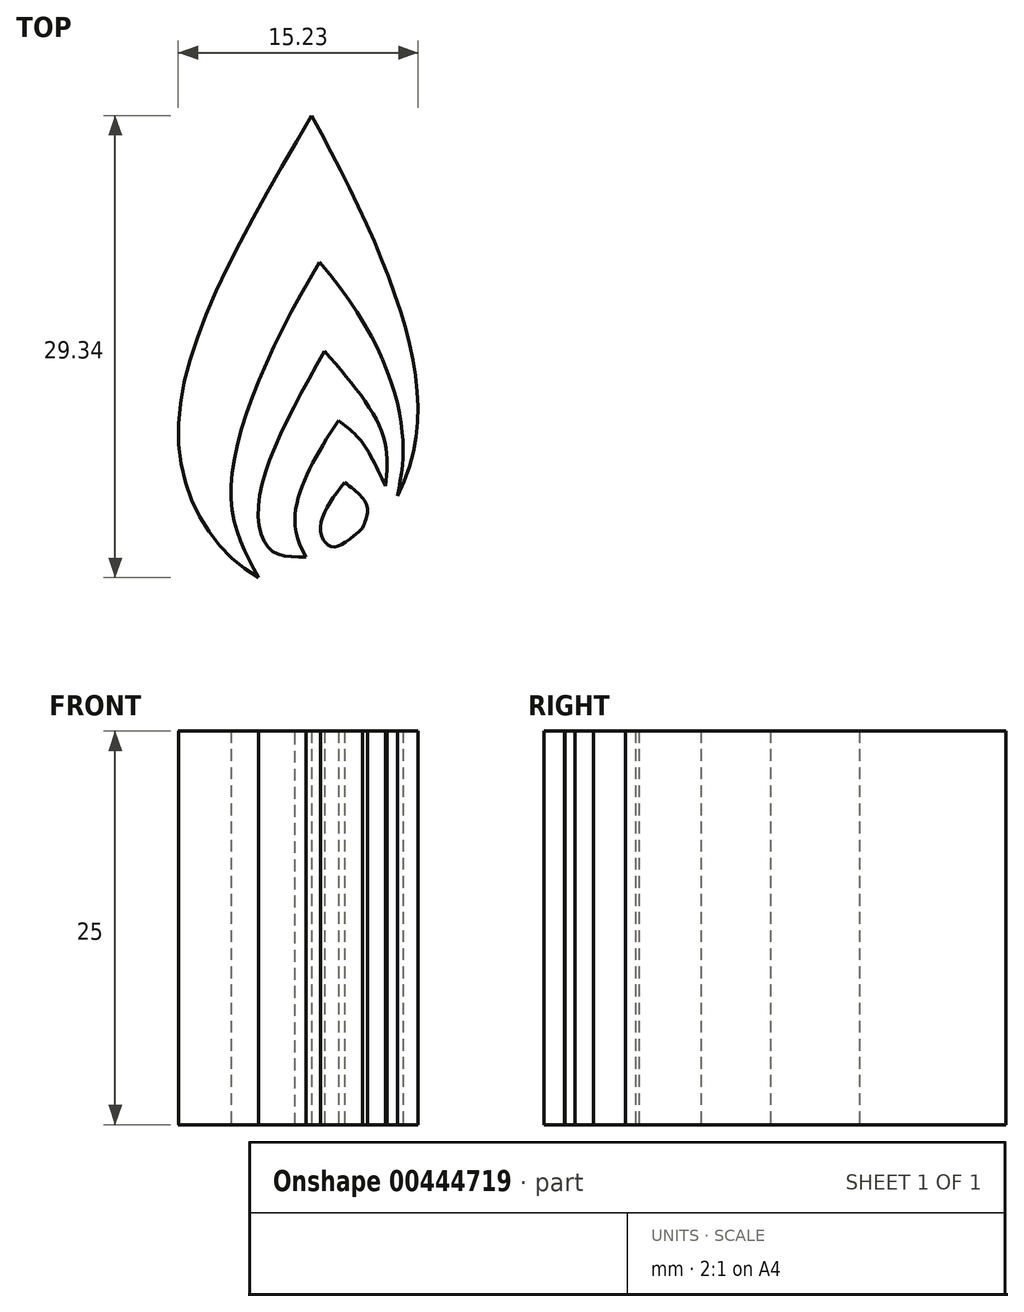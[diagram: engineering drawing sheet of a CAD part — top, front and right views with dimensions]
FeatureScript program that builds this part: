
annotation { "Feature Type Name" : "Feature", "Feature Type Description" : "" }
export const myFeature = defineFeature(function(context is Context, id is Id, definition is map)
    precondition{}
    {
        {
            var Q0;
            Q0=qCreatedBy(makeId("Top.planeOp"),FACE);
            var sketch = newSketch(context, id + "F0", { "sketchPlane" : qUnion([Q0])});
            skFitSpline(sketch, "E0", {"points": [v(-21.54, 31.4) * mm, v(-30, 10.88) * mm, v(-24.9, 2.05) * mm], "startDerivative": vector(-22.17, -38.16) * mm, "endDerivative": vector(20.91, -11.63) * mm});
            skFitSpline(sketch, "E1", {"points": [v(-21.54, 31.4) * mm, v(-15.36, 17.1) * mm, v(-16.09, 7.23) * mm], "startDerivative": vector(14.64, -26.64) * mm, "endDerivative": vector(-11.02, -21.44) * mm});
            skFitSpline(sketch, "E2", {"points": [v(-24.9, 2.05) * mm, v(-26.64, 7.68) * mm, v(-21.02, 22.09) * mm], "startDerivative": vector(-7.2, 13.11) * mm, "endDerivative": vector(14.41, 23.6) * mm});
            skFitSpline(sketch, "E3", {"points": [v(-21.02, 22.09) * mm, v(-15.84, 11.85) * mm, v(-16.09, 7.23) * mm], "startDerivative": vector(16.12, -18.6) * mm, "endDerivative": vector(-2.41, -10.96) * mm});
            skFitSpline(sketch, "E4", {"points": [v(-20.7, 16.43) * mm, v(-24.85, 7.1) * mm, v(-24.1, 3.78) * mm, v(-21.88, 3.37) * mm], "startDerivative": vector(-11.59, -20.64) * mm, "endDerivative": vector(10.8, 0.23) * mm});
            skFitSpline(sketch, "E5", {"points": [v(-20.7, 16.43) * mm, v(-17.04, 11.25) * mm, v(-16.83, 7.86) * mm], "startDerivative": vector(8.03, -9.25) * mm, "endDerivative": vector(-0.74, -7.82) * mm});
            skFitSpline(sketch, "E6", {"points": [v(-16.83, 7.86) * mm, v(-18.42, 10.76) * mm, v(-19.8, 12) * mm], "startDerivative": vector(-2.66, 5.7) * mm, "endDerivative": vector(-3.32, 2.44) * mm});
            skFitSpline(sketch, "E7", {"points": [v(-19.8, 12) * mm, v(-22.3, 7.38) * mm, v(-21.88, 3.37) * mm], "startDerivative": vector(-6.15, -8.71) * mm, "endDerivative": vector(5.78, -9.78) * mm});
            skFitSpline(sketch, "E8", {"points": [v(-19.44, 8.1) * mm, v(-18.02, 6.63) * mm, v(-18.28, 5.2) * mm], "startDerivative": vector(3.5, -2.57) * mm, "endDerivative": vector(-1.31, -3.22) * mm});
            skFitSpline(sketch, "E9", {"points": [v(-18.28, 5.2) * mm, v(-20.24, 4.01) * mm, v(-20.97, 5.2) * mm, v(-19.44, 8.1) * mm], "startDerivative": vector(-6.33, -5.77) * mm, "endDerivative": vector(5.67, 7.47) * mm});
            skSolve(sketch);
        }
        {
            var Q0;
            Q0=makeQuery(id+"F0.imprint","IMPRINT",FACE,{"disambiguationData":[TD([[makeQuery(id+"F0.imprint","IMPRINT",EDGE,{"derivedFrom":sQuery(id+"F0.wireOp",EDGE,"E4")}),1.0]])]});
            var Q1;
            Q1=makeQuery(id+"F0.imprint","IMPRINT",FACE,{"disambiguationData":[TD([[makeQuery(id+"F0.imprint","IMPRINT",EDGE,{"derivedFrom":sQuery(id+"F0.wireOp",EDGE,"E8")}),-1.0]])]});
            var Q2;
            Q2=makeQuery(id+"F0.imprint","IMPRINT",FACE,{"disambiguationData":[TD([[makeQuery(id+"F0.imprint","IMPRINT",EDGE,{"derivedFrom":sQuery(id+"F0.wireOp",EDGE,"E0")}),1.0]])]});
            extrude(context, id + "F1", {"entities" : qUnion([Q0, Q1, Q2]), "depth" : 25 * mm});
        }
    });
